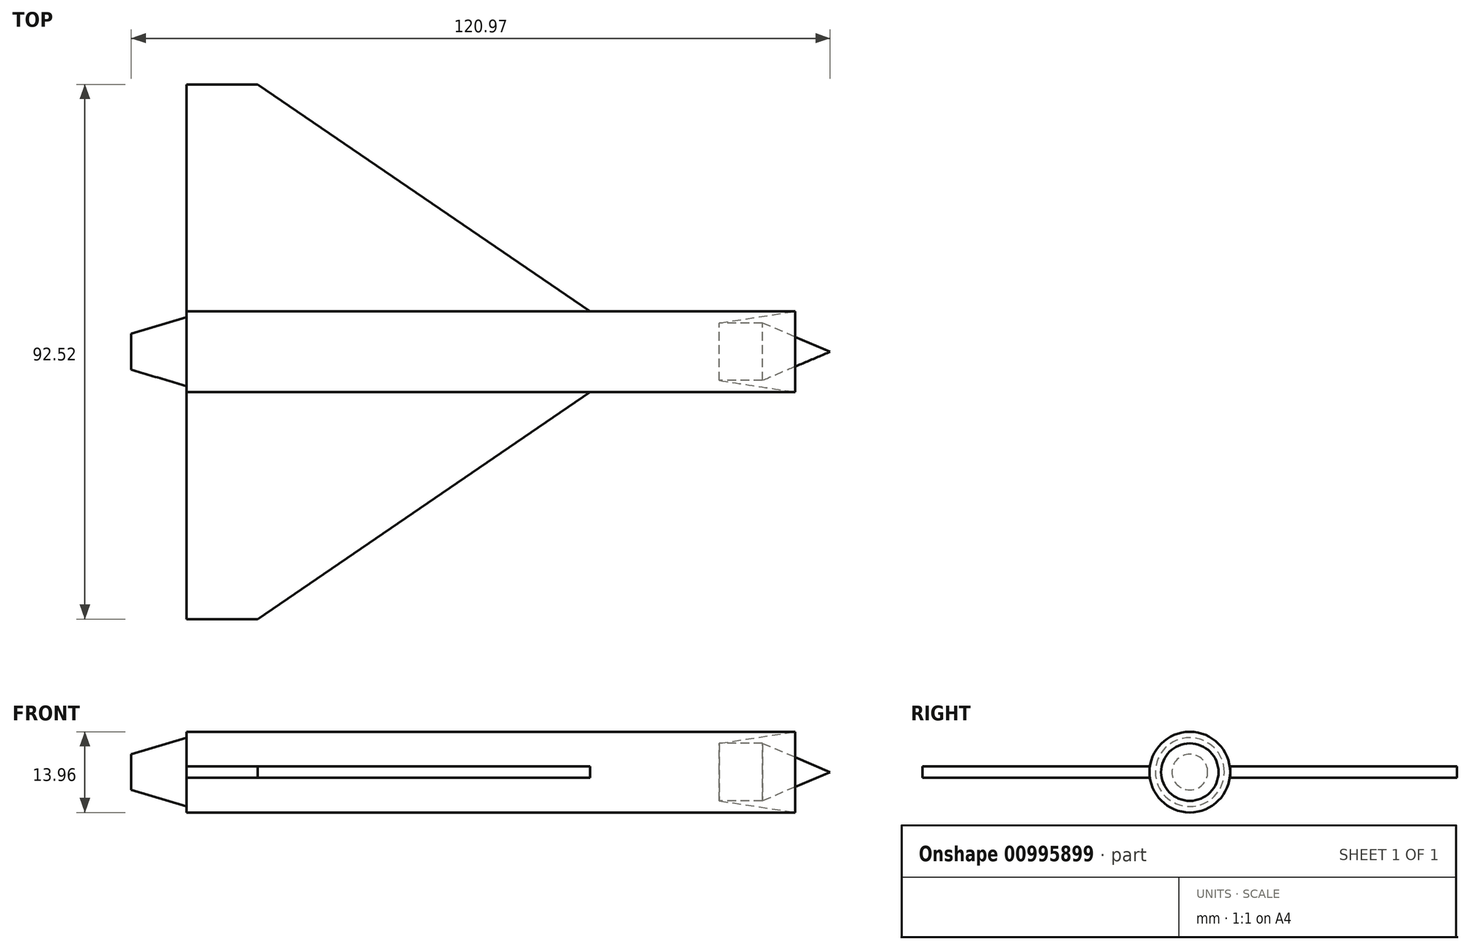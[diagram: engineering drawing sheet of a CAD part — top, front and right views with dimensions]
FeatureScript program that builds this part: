
annotation { "Feature Type Name" : "Feature", "Feature Type Description" : "" }
export const myFeature = defineFeature(function(context is Context, id is Id, definition is map)
    precondition{}
    {
        {
            var Q0;
            Q0=qCreatedBy(makeId("Top.planeOp"),FACE);
            var sketch = newSketch(context, id + "F0", { "sketchPlane" : qUnion([Q0])});
            skLineSegment(sketch, "E0", {"start": v(-60.77, 19.73) * mm, "end": v(-60.77, 16.63) * mm});
            skLineSegment(sketch, "E1", {"start": v(-51.2, 12.75) * mm, "end": v(24.66, 12.75) * mm});
            skLineSegment(sketch, "E2", {"start": v(24.66, 12.75) * mm, "end": v(33.55, 14.76) * mm});
            skLineSegment(sketch, "E3", {"start": v(33.55, 14.76) * mm, "end": v(48.5, 14.76) * mm});
            skLineSegment(sketch, "E4", {"start": v(48.5, 14.76) * mm, "end": v(60.2, 19.73) * mm});
            skLineSegment(sketch, "E5", {"start": v(-60.77, 19.73) * mm, "end": v(62.8, 19.73) * mm, "construction": true});
            skLineSegment(sketch, "E6", {"start": v(24.66, 12.75) * mm, "end": v(54.14, 12.75) * mm});
            skLineSegment(sketch, "E7", {"start": v(54.14, 12.75) * mm, "end": v(41.03, 14.76) * mm});
            skLineSegment(sketch, "E8", {"start": v(-51.2, 12.75) * mm, "end": v(-51.2, 13.77) * mm});
            skLineSegment(sketch, "E9", {"start": v(-51.2, 13.77) * mm, "end": v(-60.77, 16.63) * mm});
            skLineSegment(sketch, "E10", {"start": v(-60.77, 19.73) * mm, "end": v(60.2, 19.73) * mm});
            skSolve(sketch);
        }
        {
            var Q0;
            Q0=makeQuery(id+"F0.imprint","IMPRINT",FACE,{"disambiguationData":[TD([[makeQuery(id+"F0.imprint","IMPRINT",EDGE,{"derivedFrom":sQuery(id+"F0.wireOp",EDGE,"E0")}),1.0]])]});
            var Q1;
            {var subQ0=sQuery(id+"F0.wireOp",EDGE,"E2");Q1=makeQuery(id+"F0.imprint","IMPRINT",FACE,{"disambiguationData":[TD([[makeQuery(id+"F0.imprint","IMPRINT",EDGE,{"derivedFrom":subQ0}),-1.0]])]});}
            var Q2;
            Q2=sQuery(id+"F0.wireOp",EDGE,"E10");
            revolve(context, id + "F1", {"surfaceOperationType" : NewSurfaceOperationType.NEW, "entities" : qUnion([Q0, Q1]), "axis" : qUnion([Q2]), "revolveType" : RevolveType.FULL});
        }
        {
            var Q0;
            Q0=qCreatedBy(makeId("Top.planeOp"),FACE);
            var sketch = newSketch(context, id + "F2", { "sketchPlane" : qUnion([Q0])});
            skLineSegment(sketch, "E11", {"start": v(-51.2, 26.7) * mm, "end": v(54.14, 26.7) * mm});
            skLineSegment(sketch, "E12", {"start": v(54.14, 12.75) * mm, "end": v(-51.2, 12.75) * mm});
            skLineSegment(sketch, "E13", {"start": v(-51.2, 26.7) * mm, "end": v(-51.2, 65.99) * mm});
            skLineSegment(sketch, "E14", {"start": v(-51.2, 65.99) * mm, "end": v(-38.9, 65.99) * mm});
            skLineSegment(sketch, "E15", {"start": v(-38.9, 65.99) * mm, "end": v(18.66, 26.7) * mm});
            skPoint(sketch, "E16.0", {"position": v(60.2, 19.73) * mm});
            skLineSegment(sketch, "E17.0", {"start": v(-60.77, 16.63) * mm, "end": v(-60.77, 22.83) * mm, "construction": true});
            skPoint(sketch, "E18", {"position": v(-60.77, 19.73) * mm});
            skLineSegment(sketch, "E19", {"start": v(-60.77, 19.73) * mm, "end": v(60.2, 19.73) * mm, "construction": true});
            skLineSegment(sketch, "E20.MirrorCS", {"start": v(-38.9, -26.53) * mm, "end": v(18.66, 12.75) * mm});
            skLineSegment(sketch, "E21.MirrorCS", {"start": v(-51.2, -26.53) * mm, "end": v(-38.9, -26.53) * mm});
            skLineSegment(sketch, "E22.MirrorCS", {"start": v(-51.2, 12.75) * mm, "end": v(-51.2, -26.53) * mm});
            skSolve(sketch);
        }
        {
            var Q0;
            {var subQ0=sQuery(id+"F2.wireOp",EDGE,"E13");Q0=makeQuery(id+"F2.imprint","IMPRINT",FACE,{"disambiguationData":[TD([[makeQuery(id+"F2.imprint","IMPRINT",EDGE,{"derivedFrom":subQ0}),-1.0]])]});}
            var Q1;
            {var subQ2=sQuery(id+"F2.wireOp",EDGE,"E20.MirrorCS");Q1=makeQuery(id+"F2.imprint","IMPRINT",FACE,{"disambiguationData":[TD([[makeQuery(id+"F2.imprint","IMPRINT",EDGE,{"derivedFrom":subQ2}),1.0]])]});}
            extrude(context, id + "F3", {"entities" : qUnion([Q0, Q1]), "operationType" : NewBodyOperationType.ADD, "depth" : 1 * mm, "offsetDistance" : 25 * mm, "hasSecondDirection" : true, "secondDirectionOppositeDirection" : true, "secondDirectionDepth" : 1 * mm});
        }
        {
            var Q0;
            Q0=qCreatedBy(makeId("Front.planeOp"),FACE);
            var Q1;
            Q1=makeQuery(id+"F1.opRevolve","SWEPT_VERTEX",VERTEX,{"disambiguationData":[OSD([sQuery(id+"F0.wireOp",EDGE,"E4"),sQuery(id+"F0.wireOp",EDGE,"E10")])]});
            cPlane(context, id + "F4", {"entities" : qUnion([Q0, Q1]), "cplaneType" : CPlaneType.PLANE_POINT, "offset" : 25 * mm, "width" : 150 * mm, "height" : 150 * mm});
        }
    });
